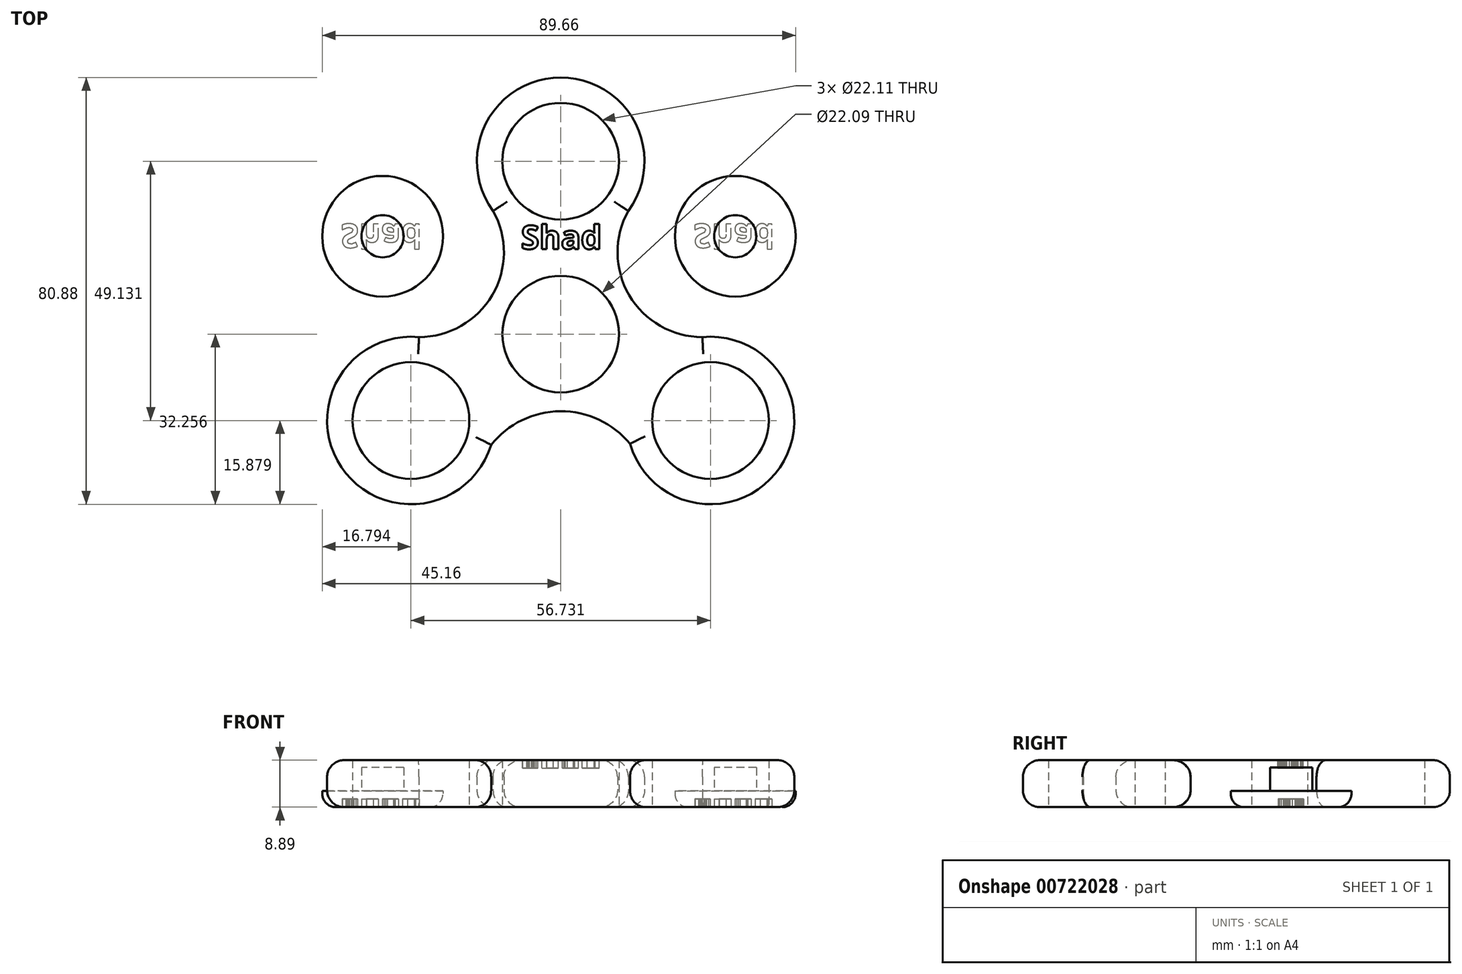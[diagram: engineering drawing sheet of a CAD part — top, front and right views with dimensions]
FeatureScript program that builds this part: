
annotation { "Feature Type Name" : "Feature", "Feature Type Description" : "" }
export const myFeature = defineFeature(function(context is Context, id is Id, definition is map)
    precondition{}
    {
        {
            var Q0;
            Q0=qCreatedBy(makeId("Top.planeOp"),FACE);
            var sketch = newSketch(context, id + "F0", { "sketchPlane" : qUnion([Q0])});
            skCircle(sketch, "E0", {"center": v(0, 61.7) * mm, "radius": 11.06 * mm});
            skCircle(sketch, "E1.1.0", {"center": v(-28.37, 12.58) * mm, "radius": 11.06 * mm});
            skCircle(sketch, "E1.2.0", {"center": v(28.37, 12.58) * mm, "radius": 11.06 * mm});
            skPoint(sketch, "E1.center", {"position": v(0, 28.96) * mm});
            skCircle(sketch, "E2", {"center": v(0, 28.96) * mm, "radius": 11.04 * mm});
            skArc(sketch, "E3", {"start": v(12.8, 52.32) * mm, "mid": v(0, 77.58) * mm, "end": v(-12.8, 52.32) * mm});
            skArc(sketch, "E4", {"start": v(-26.83, 28.38) * mm, "mid": v(-41.56, 3.75) * mm, "end": v(-13.17, 7.97) * mm});
            skArc(sketch, "E5", {"start": v(13.12, 8.14) * mm, "mid": v(41.51, 3.68) * mm, "end": v(26.83, 28.38) * mm});
            skArc(sketch, "E6", {"start": v(-26.83, 28.38) * mm, "mid": v(-12.5, 37.21) * mm, "end": v(-13.87, 54) * mm});
            skArc(sketch, "E7.MirrorCS", {"start": v(26.83, 28.38) * mm, "mid": v(12.5, 37.21) * mm, "end": v(13.87, 54) * mm});
            skArc(sketch, "E8", {"start": v(16.22, 2.35) * mm, "mid": v(0.13, 14.33) * mm, "end": v(-16.08, 2.52) * mm});
            skSolve(sketch);
        }
        {
            var Q0;
            Q0 = qSketchRegion(id + "F0", true);
            extrude(context, id + "F1", {"entities" : qUnion([Q0]), "depth" : 8.9 * mm, "offsetDistance" : 25.4 * mm});
        }
        {
            var Q0;
            Q0=makeQuery(id+"F1.opExtrude","CAP_EDGE",EDGE,{"disambiguationData":[OSD([sQuery(id+"F0.wireOp",EDGE,"E8")])],"isStart":false});
            var Q1;
            Q1=makeQuery(id+"F1.opExtrude","CAP_EDGE",EDGE,{"disambiguationData":[OSD([sQuery(id+"F0.wireOp",EDGE,"E4")])],"isStart":false});
            var Q2;
            Q2=makeQuery(id+"F1.opExtrude","CAP_EDGE",EDGE,{"disambiguationData":[OSD([sQuery(id+"F0.wireOp",EDGE,"E6")])],"isStart":false});
            var Q3;
            Q3=makeQuery(id+"F1.opExtrude","CAP_EDGE",EDGE,{"disambiguationData":[OSD([sQuery(id+"F0.wireOp",EDGE,"E3")])],"isStart":false});
            var Q4;
            Q4=makeQuery(id+"F1.opExtrude","CAP_EDGE",EDGE,{"disambiguationData":[OSD([sQuery(id+"F0.wireOp",EDGE,"E5")])],"isStart":false});
            var Q5;
            Q5=makeQuery(id+"F1.opExtrude","CAP_EDGE",EDGE,{"disambiguationData":[OSD([sQuery(id+"F0.wireOp",EDGE,"E7.MirrorCS")])],"isStart":false});
            var Q6;
            Q6=makeQuery(id+"F1.opExtrude","CAP_EDGE",EDGE,{"disambiguationData":[OSD([sQuery(id+"F0.wireOp",EDGE,"E7.MirrorCS")])],"isStart":true});
            var Q7;
            Q7=makeQuery(id+"F1.opExtrude","CAP_EDGE",EDGE,{"disambiguationData":[OSD([sQuery(id+"F0.wireOp",EDGE,"E3")])],"isStart":true});
            var Q8;
            Q8=makeQuery(id+"F1.opExtrude","CAP_EDGE",EDGE,{"disambiguationData":[OSD([sQuery(id+"F0.wireOp",EDGE,"E5")])],"isStart":true});
            var Q9;
            Q9=makeQuery(id+"F1.opExtrude","CAP_EDGE",EDGE,{"disambiguationData":[OSD([sQuery(id+"F0.wireOp",EDGE,"E8")])],"isStart":true});
            var Q10;
            Q10=makeQuery(id+"F1.opExtrude","CAP_EDGE",EDGE,{"disambiguationData":[OSD([sQuery(id+"F0.wireOp",EDGE,"E4")])],"isStart":true});
            var Q11;
            Q11=makeQuery(id+"F1.opExtrude","CAP_EDGE",EDGE,{"disambiguationData":[OSD([sQuery(id+"F0.wireOp",EDGE,"E6")])],"isStart":true});
            fillet(context, id + "F2", {"entities" : qUnion([Q0, Q1, Q2, Q3, Q4, Q5, Q6, Q7, Q8, Q9, Q10, Q11]), "radius" : 3.17 * mm, "tangentPropagation" : true, "allowEdgeOverflow" : false});
        }
        {
            var Q0;
            Q0=qCreatedBy(makeId("Top.planeOp"),FACE);
            var sketch = newSketch(context, id + "F3", { "sketchPlane" : qUnion([Q0])});
            skCircle(sketch, "E9", {"center": v(33.07, 47.5) * mm, "radius": 11.43 * mm});
            skSolve(sketch);
        }
        {
            var Q0;
            Q0=makeQuery(id+"F3.imprint","IMPRINT",FACE,{"disambiguationData":[TD([[makeQuery(id+"F3.imprint","IMPRINT",EDGE,{"derivedFrom":sQuery(id+"F3.wireOp",EDGE,"E9")}),1.0]])]});
            extrude(context, id + "F4", {"entities" : qUnion([Q0]), "depth" : 3.05 * mm, "offsetDistance" : 25.4 * mm});
        }
        {
            var Q0;
            Q0=makeQuery(id+"F4.opExtrude","CAP_FACE",FACE,{"disambiguationData":[OSD([sQuery(id+"F3.wireOp",EDGE,"E9")])],"isStart":false});
            var sketch = newSketch(context, id + "F5", { "sketchPlane" : qUnion([Q0])});
            skCircle(sketch, "E10", {"center": v(33.07, 47.5) * mm, "radius": 4 * mm});
            skSolve(sketch);
        }
        {
            var Q0;
            Q0=makeQuery(id+"F5.imprint","IMPRINT",FACE,{"disambiguationData":[TD([[makeQuery(id+"F5.imprint","IMPRINT",EDGE,{"derivedFrom":sQuery(id+"F5.wireOp",EDGE,"E10")}),1.0]])]});
            extrude(context, id + "F6", {"entities" : qUnion([Q0]), "operationType" : NewBodyOperationType.ADD, "depth" : 4.44 * mm, "offsetDistance" : 25.4 * mm});
        }
        {
            var Q0;
            Q0=makeQuery(id+"F4.opExtrude","CAP_EDGE",EDGE,{"disambiguationData":[OSD([sQuery(id+"F3.wireOp",EDGE,"E9")])],"isStart":true});
            fillet(context, id + "F7", {"entities" : qUnion([Q0]), "radius" : 2.54 * mm, "tangentPropagation" : true, "allowEdgeOverflow" : false});
        }
        {
            var Q0;
            Q0=makeQuery(id+"F4.opExtrude","CAP_FACE",FACE,{"disambiguationData":[OSD([sQuery(id+"F3.wireOp",EDGE,"E9")])],"isStart":true});
            var sketch = newSketch(context, id + "F8", { "sketchPlane" : qUnion([Q0])});
            skText(sketch, "E11", { "text": "Shad", "fontName": "OpenSans-Bold.ttf"});
            const initialGuessF8  = {"E11": [0.02513, -0.04983, 1, 0, 0.00453]};
            skSetInitialGuess(sketch, initialGuessF8);
            skSolve(sketch);
        }
        {
            var Q0;
            Q0 = qSketchRegion(id + "F8", true);
            extrude(context, id + "F9", {"entities" : qUnion([Q0]), "operationType" : NewBodyOperationType.REMOVE, "oppositeDirection" : true, "depth" : 1.52 * mm, "offsetDistance" : 25.4 * mm});
        }
        {
            var Q0;
            Q0=makeQuery(id+"F4.opExtrude","SWEPT_BODY",BODY,{"disambiguationData":[OSD([sQuery(id+"F3.wireOp",EDGE,"E9")])]});
            transform(context, id + "F10", {"entities" : qUnion([Q0]), "transformType" : TransformType.TRANSLATION_3D, "dx" : -66.8 * mm, "dy" : 0 * mm, "dz" : 0 * mm, "makeCopy" : true});
        }
        {
            var Q0;
            Q0=makeQuery(id+"F1.opExtrude","CAP_FACE",FACE,{"disambiguationData":[OSD([sQuery(id+"F0.wireOp",EDGE,"E0"),sQuery(id+"F0.wireOp",EDGE,"E1.1.0"),sQuery(id+"F0.wireOp",EDGE,"E1.2.0"),sQuery(id+"F0.wireOp",EDGE,"E2"),sQuery(id+"F0.wireOp",EDGE,"E3"),sQuery(id+"F0.wireOp",EDGE,"E4"),sQuery(id+"F0.wireOp",EDGE,"E5"),sQuery(id+"F0.wireOp",EDGE,"E6"),sQuery(id+"F0.wireOp",EDGE,"E7.MirrorCS"),sQuery(id+"F0.wireOp",EDGE,"E8")])],"isStart":false});
            var sketch = newSketch(context, id + "F11", { "sketchPlane" : qUnion([Q0])});
            skText(sketch, "E12", { "text": "Shad", "fontName": "OpenSans-Bold.ttf"});
            const initialGuessF11  = {"E12": [-0.00752, 0.04507, 1, 0, 0.0045]};
            skSetInitialGuess(sketch, initialGuessF11);
            skSolve(sketch);
        }
        {
            var Q0;
            Q0 = qSketchRegion(id + "F11", true);
            extrude(context, id + "F12", {"entities" : qUnion([Q0]), "operationType" : NewBodyOperationType.REMOVE, "oppositeDirection" : true, "depth" : 1.52 * mm, "offsetDistance" : 25.4 * mm});
        }
    });
